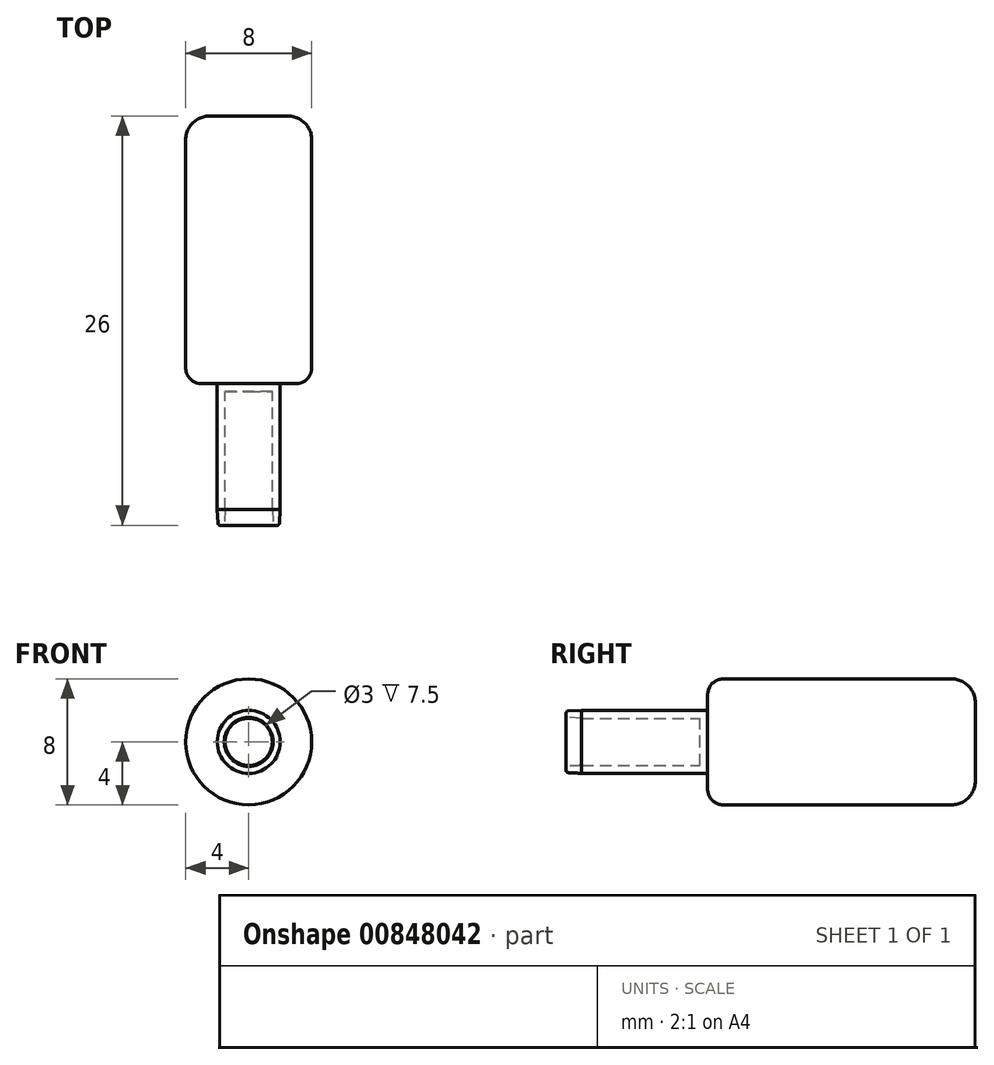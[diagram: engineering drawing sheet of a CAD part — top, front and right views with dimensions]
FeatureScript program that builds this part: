
annotation { "Feature Type Name" : "Feature", "Feature Type Description" : "" }
export const myFeature = defineFeature(function(context is Context, id is Id, definition is map)
    precondition{}
    {
        {
            var Q0;
            Q0=qCreatedBy(makeId("Front.planeOp"),FACE);
            var sketch = newSketch(context, id + "F0", { "sketchPlane" : qUnion([Q0])});
            skCircle(sketch, "E0", {"center": v(0, 0) * mm, "radius": 2 * mm});
            skSolve(sketch);
        }
        {
            var Q0;
            Q0=makeQuery(id+"F0.imprint","IMPRINT",FACE,{"disambiguationData":[TD([[makeQuery(id+"F0.imprint","IMPRINT",EDGE,{"derivedFrom":sQuery(id+"F0.wireOp",EDGE,"E0")}),1.0]])]});
            extrude(context, id + "F1", {"entities" : qUnion([Q0]), "depth" : 8 * mm, "offsetDistance" : 25 * mm});
        }
        {
            var Q0;
            Q0=makeQuery(id+"F1.opExtrude","CAP_FACE",FACE,{"disambiguationData":[OSD([sQuery(id+"F0.wireOp",EDGE,"E0")])],"isStart":false});
            shell(context, id + "F2", {"entities" : qUnion([Q0]), "thickness" : .5 * mm});
        }
        {
            var Q0;
            Q0=makeQuery(id+"F1.opExtrude","CAP_FACE",FACE,{"disambiguationData":[OSD([sQuery(id+"F0.wireOp",EDGE,"E0")])],"isStart":false});
            extrude(context, id + "F3", {"entities" : qUnion([Q0]), "operationType" : NewBodyOperationType.ADD, "depth" : 1 * mm, "offsetDistance" : 25 * mm, "hasDraft" : true, "draftAngle" : 3 * degree, "draftPullDirection" : true});
        }
        {
            var Q0;
            {var subQ0=sQuery(id+"F0.wireOp",EDGE,"E0");Q0=makeQuery(id+"F3.opExtrude","CAP_EDGE",EDGE,{"disambiguationData":[OSD([subQ0]),TDD([makeQuery(id+"F1.opExtrude","CAP_EDGE",EDGE,{"disambiguationData":[OSD([subQ0])],"isStart":false})])],"isStart":false});}
            fillet(context, id + "F4", {"entities" : qUnion([Q0]), "radius" : .15 * mm, "tangentPropagation" : true, "allowEdgeOverflow" : false});
        }
        {
            var Q0;
            Q0=qCreatedBy(makeId("Front.planeOp"),FACE);
            var sketch = newSketch(context, id + "F5", { "sketchPlane" : qUnion([Q0])});
            skCircle(sketch, "E1", {"center": v(0, 0) * mm, "radius": 4 * mm});
            skSolve(sketch);
        }
        {
            var Q0;
            Q0=makeQuery(id+"F5.imprint","IMPRINT",FACE,{"disambiguationData":[TD([[makeQuery(id+"F5.imprint","IMPRINT",EDGE,{"derivedFrom":sQuery(id+"F5.wireOp",EDGE,"E1")}),1.0]])]});
            extrude(context, id + "F6", {"entities" : qUnion([Q0]), "operationType" : NewBodyOperationType.ADD, "oppositeDirection" : true, "depth" : 17 * mm, "offsetDistance" : 25 * mm});
        }
        {
            var Q0;
            Q0=makeQuery(id+"F6.opExtrude","CAP_EDGE",EDGE,{"disambiguationData":[OSD([sQuery(id+"F5.wireOp",EDGE,"E1")])],"isStart":true});
            fillet(context, id + "F7", {"entities" : qUnion([Q0]), "radius" : 1 * mm, "tangentPropagation" : true, "allowEdgeOverflow" : false});
        }
        {
            var Q0;
            Q0=makeQuery(id+"F6.opExtrude","CAP_EDGE",EDGE,{"disambiguationData":[OSD([sQuery(id+"F5.wireOp",EDGE,"E1")])],"isStart":false});
            fillet(context, id + "F8", {"entities" : qUnion([Q0]), "radius" : 1.5 * mm, "tangentPropagation" : true, "allowEdgeOverflow" : false});
        }
    });
